# Revit family: Fountain-Eyewash-Bradley_Corp-S19-304
name_source: partatom
category: Plumbing Fixtures
revit_build: Autodesk Revit 2015 (Build: 20140223_1515(x64)
units: mm (PartAtom-declared; Revit-internal decimal feet)

## types (1)
- S19-304
    Apparent Load = 0 VA
    Assembly Code = D2010
    BRADTECT® Safety Coating = Plastic - Bradley Corp - Safety Yellow
    Barrier-Free = No
    Bottom of Showerhead = 85 1/4"
    CWFU = 0
    Chrome-plated red brass = Metal - Bradley Corp - Chrome
    Class 1, Div 1, Groups C & D = No
    Class 1, Div2, Groups B,C,D = No
    Cold Water Connection Diameter = 1"
    Cold Water Connection Radius = 1"
    Default Elevation = 48"
    Description = Heat Trace Emergency Shower and Eye/Face Wash Unit
    Drain Pipe = Yes
    Fixture Material = Metal - Bradley Corp - Stainless Steel
    Flow Pressure = 0.00 psi
    Foot Pedal = No
    Halo Eye/Fase Wash = No
    Halo Eyewash = Yes
    Height = 94 5/8"
    Industry Standards = ANSI/ISEA Z358.1, cCSAus Listed, NEMA 4X Standard
    Length = 37 3/4"
    Manufacturer = Bradley Corporation
    Manufacturer Installation URL - English = https://www.bradleycorp.com
    MasterFormat Number = 22 45 13
    MasterFormat Title = Emergency Showers
    Model = S19-304
    Navigator EFX25 Emergency Thermostat Mixing Valve = Yes
    Number of Poles = 1
    OmniClass Code = 23-29 37 15 11
    OmniClass Table 23 Number = 23-29 37 15 11
    OmniClass Table 23 Title = Combination Emergency Showers
    OmniClass Title = Combination Emergency Showers
    Percentage of Recycled Content = 0
    Pipe Material = Metal - Bradley Corp - BRADTECT® Safety Yellow Coating
    Plastic Dust Cover = Yes
    Plastic Material = Plastic - Bradley Corp - Black
    Power Factor = 0
    Product Page URL = https://www.bradleycorp.com
    Product Tech Data URL - English = https://www.bradleycorp.com
    SS Bowl = Yes
    SS Dust Cover = No
    Specifications URL = https://www.bradleycorp.com
    Stainless Steel = Metal - Bradley Corp - Stainless Steel
    URL = http://www.bradleycorp.com
    Version = 1.0
    Warranty Information = Full, One-Year
    Width = 19 1/4"

## geometry (parser evidence)
native form markers: Blend x8, Sweep x13
no freeform markers — native parametric forms only
